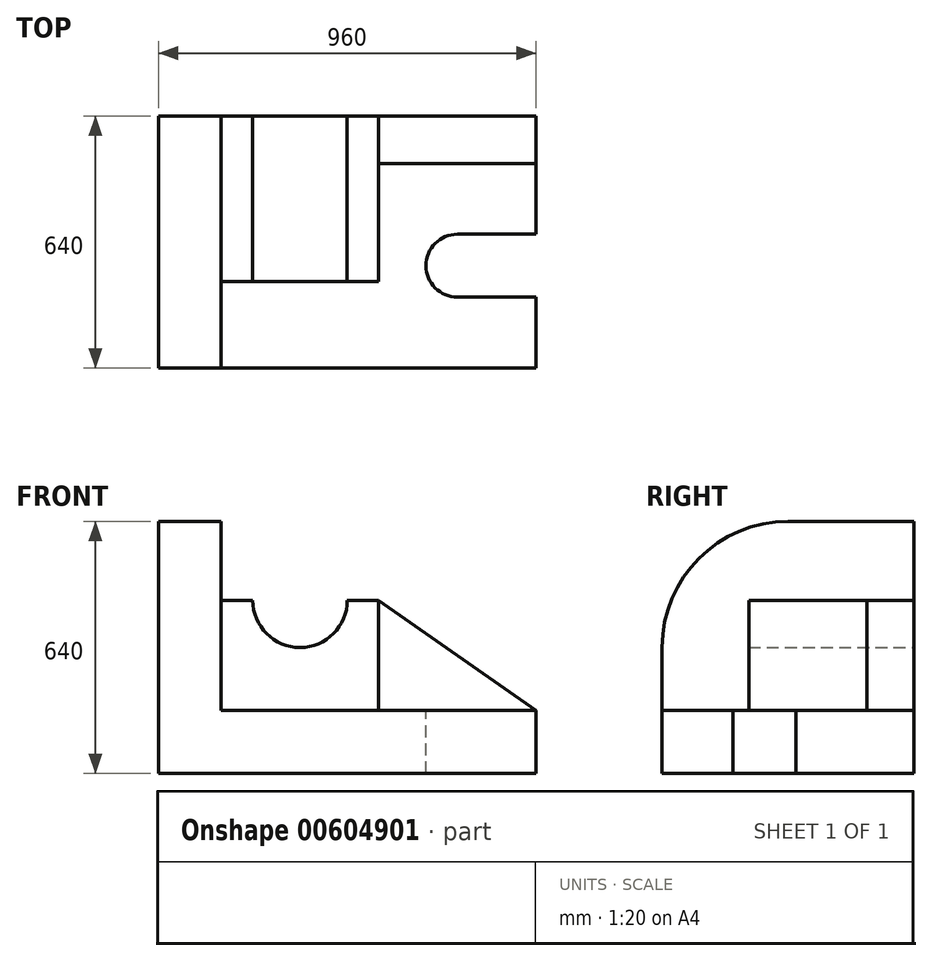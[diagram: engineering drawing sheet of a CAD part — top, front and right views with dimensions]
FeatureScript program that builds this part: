
annotation { "Feature Type Name" : "Feature", "Feature Type Description" : "" }
export const myFeature = defineFeature(function(context is Context, id is Id, definition is map)
    precondition{}
    {
        {
            var Q0;
            Q0=qCreatedBy(makeId("Top.planeOp"),FACE);
            var sketch = newSketch(context, id + "F0", { "sketchPlane" : qUnion([Q0])});
            skLineSegment(sketch, "E0.bottom", {"start": v(-911.97, 609.27) * mm, "end": v(48.03, 609.27) * mm});
            skLineSegment(sketch, "E0.top", {"start": v(-911.97, -30.73) * mm, "end": v(48.03, -30.73) * mm});
            skLineSegment(sketch, "E0.left", {"start": v(-911.97, 609.27) * mm, "end": v(-911.97, -30.73) * mm});
            skLineSegment(sketch, "E0.right", {"start": v(48.03, 609.27) * mm, "end": v(48.03, -30.73) * mm});
            skSolve(sketch);
        }
        {
            var Q0;
            Q0 = qSketchRegion(id + "F0", true);
            extrude(context, id + "F1", {"entities" : qUnion([Q0]), "depth" : 160 * mm, "offsetDistance" : 25 * mm});
        }
        {
            var Q0;
            Q0=makeQuery(id+"F1.opExtrude","SWEPT_FACE",FACE,{"disambiguationData":[OSD([sQuery(id+"F0.wireOp",EDGE,"E0.left")])]});
            var sketch = newSketch(context, id + "F2", { "sketchPlane" : qUnion([Q0])});
            skLineSegment(sketch, "E1", {"start": v(-609.27, 160) * mm, "end": v(-609.27, 640) * mm});
            skLineSegment(sketch, "E2", {"start": v(-609.27, 640) * mm, "end": v(-289.27, 640) * mm});
            skLineSegment(sketch, "E3", {"start": v(30.73, 160) * mm, "end": v(30.73, 320) * mm});
            skArc(sketch, "E4", {"start": v(30.73, 320) * mm, "mid": v(-63, 546.27) * mm, "end": v(-289.27, 640) * mm});
            skSolve(sketch);
        }
        {
            var Q0;
            Q0=makeQuery(id+"F2.imprint","IMPRINT",FACE,{"disambiguationData":[TD([[makeQuery(id+"F2.imprint","IMPRINT",EDGE,{"derivedFrom":sQuery(id+"F2.wireOp",EDGE,"E1")}),-1.0]])]});
            extrude(context, id + "F3", {"entities" : qUnion([Q0]), "operationType" : NewBodyOperationType.ADD, "oppositeDirection" : true, "depth" : 160 * mm, "offsetDistance" : 25 * mm});
        }
        {
            var Q0;
            Q0=makeQuery(id+"F3.boolean.opBoolean","MERGE",FACE,{"derivedFrom":[makeQuery(id+"F1.opExtrude","SWEPT_FACE",FACE,{"disambiguationData":[OSD([sQuery(id+"F0.wireOp",EDGE,"E0.bottom")])]}),makeQuery(id+"F3.opExtrude","SWEPT_FACE",FACE,{"disambiguationData":[OSD([sQuery(id+"F2.wireOp",EDGE,"E1")])]})]});
            var sketch = newSketch(context, id + "F4", { "sketchPlane" : qUnion([Q0])});
            skLineSegment(sketch, "E5", {"start": v(751.97, 160) * mm, "end": v(751.97, 440) * mm});
            skLineSegment(sketch, "E6", {"start": v(751.97, 440) * mm, "end": v(671.97, 440) * mm});
            skLineSegment(sketch, "E7", {"start": v(-48.03, 160) * mm, "end": v(351.97, 160) * mm});
            skLineSegment(sketch, "E8", {"start": v(351.97, 160) * mm, "end": v(351.97, 440) * mm});
            skLineSegment(sketch, "E9", {"start": v(351.97, 440) * mm, "end": v(-48.03, 160) * mm});
            skLineSegment(sketch, "E10", {"start": v(351.97, 440) * mm, "end": v(431.97, 440) * mm});
            skArc(sketch, "E11", {"start": v(431.97, 440) * mm, "mid": v(551.97, 320) * mm, "end": v(671.97, 440) * mm});
            skSolve(sketch);
        }
        {
            var Q0;
            Q0=makeQuery(id+"F4.imprint","IMPRINT",FACE,{"disambiguationData":[TD([[makeQuery(id+"F4.imprint","IMPRINT",EDGE,{"derivedFrom":sQuery(id+"F4.wireOp",EDGE,"E7")}),-1.0]])]});
            extrude(context, id + "F5", {"entities" : qUnion([Q0]), "operationType" : NewBodyOperationType.ADD, "oppositeDirection" : true, "depth" : 120 * mm, "offsetDistance" : 25 * mm});
        }
        {
            var Q0;
            Q0=makeQuery(id+"F5.boolean.opBoolean","MERGE",FACE,{"derivedFrom":[makeQuery(id+"F3.boolean.opBoolean","MERGE",FACE,{"derivedFrom":[makeQuery(id+"F1.opExtrude","SWEPT_FACE",FACE,{"disambiguationData":[OSD([sQuery(id+"F0.wireOp",EDGE,"E0.bottom")])]}),makeQuery(id+"F3.opExtrude","SWEPT_FACE",FACE,{"disambiguationData":[OSD([sQuery(id+"F2.wireOp",EDGE,"E1")])]})]}),makeQuery(id+"F5.opExtrude","CAP_FACE",FACE,{"disambiguationData":[OSD([sQuery(id+"F4.wireOp",EDGE,"E7"),sQuery(id+"F4.wireOp",EDGE,"E8"),sQuery(id+"F4.wireOp",EDGE,"E9")])],"isStart":true})]});
            var sketch = newSketch(context, id + "F6", { "sketchPlane" : qUnion([Q0])});
            skLineSegment(sketch, "E12", {"start": v(351.97, 440) * mm, "end": v(431.97, 440) * mm});
            skLineSegment(sketch, "E13", {"start": v(751.97, 160) * mm, "end": v(751.97, 440) * mm});
            skLineSegment(sketch, "E14", {"start": v(751.97, 440) * mm, "end": v(671.97, 440) * mm});
            skArc(sketch, "E15", {"start": v(431.97, 440) * mm, "mid": v(551.97, 320) * mm, "end": v(671.97, 440) * mm});
            skSolve(sketch);
        }
        {
            var Q0;
            Q0=makeQuery(id+"F6.imprint","IMPRINT",FACE,{"disambiguationData":[TD([[makeQuery(id+"F6.imprint","IMPRINT",EDGE,{"derivedFrom":sQuery(id+"F6.wireOp",EDGE,"E12")}),-1.0]])]});
            extrude(context, id + "F7", {"entities" : qUnion([Q0]), "operationType" : NewBodyOperationType.ADD, "oppositeDirection" : true, "depth" : 420 * mm, "offsetDistance" : 25 * mm});
        }
        {
            var Q0;
            Q0=makeQuery(id+"F1.opExtrude","CAP_FACE",FACE,{"disambiguationData":[OSD([sQuery(id+"F0.wireOp",EDGE,"E0.bottom"),sQuery(id+"F0.wireOp",EDGE,"E0.top"),sQuery(id+"F0.wireOp",EDGE,"E0.left"),sQuery(id+"F0.wireOp",EDGE,"E0.right")])],"isStart":false});
            var sketch = newSketch(context, id + "F8", { "sketchPlane" : qUnion([Q0])});
            skLineSegment(sketch, "E16", {"start": v(48.03, -30.73) * mm, "end": v(48.03, 149.27) * mm});
            skLineSegment(sketch, "E17", {"start": v(48.03, 149.27) * mm, "end": v(-151.97, 149.27) * mm});
            skLineSegment(sketch, "E18", {"start": v(48.03, 489.27) * mm, "end": v(48.03, 309.27) * mm});
            skLineSegment(sketch, "E19", {"start": v(48.03, 309.27) * mm, "end": v(-151.97, 309.27) * mm});
            skArc(sketch, "E20", {"start": v(-151.97, 309.27) * mm, "mid": v(-231.97, 229.27) * mm, "end": v(-151.97, 149.27) * mm});
            skSolve(sketch);
        }
        {
            var Q0;
            {var subQ0=sQuery(id+"F8.wireOp",EDGE,"E17");Q0=makeQuery(id+"F8.imprint","IMPRINT",FACE,{"disambiguationData":[TD([[makeQuery(id+"F8.imprint","IMPRINT",EDGE,{"derivedFrom":subQ0}),-1.0]])]});}
            extrude(context, id + "F9", {"entities" : qUnion([Q0]), "operationType" : NewBodyOperationType.REMOVE, "oppositeDirection" : true, "depth" : 160 * mm, "offsetDistance" : 25 * mm});
        }
    });
